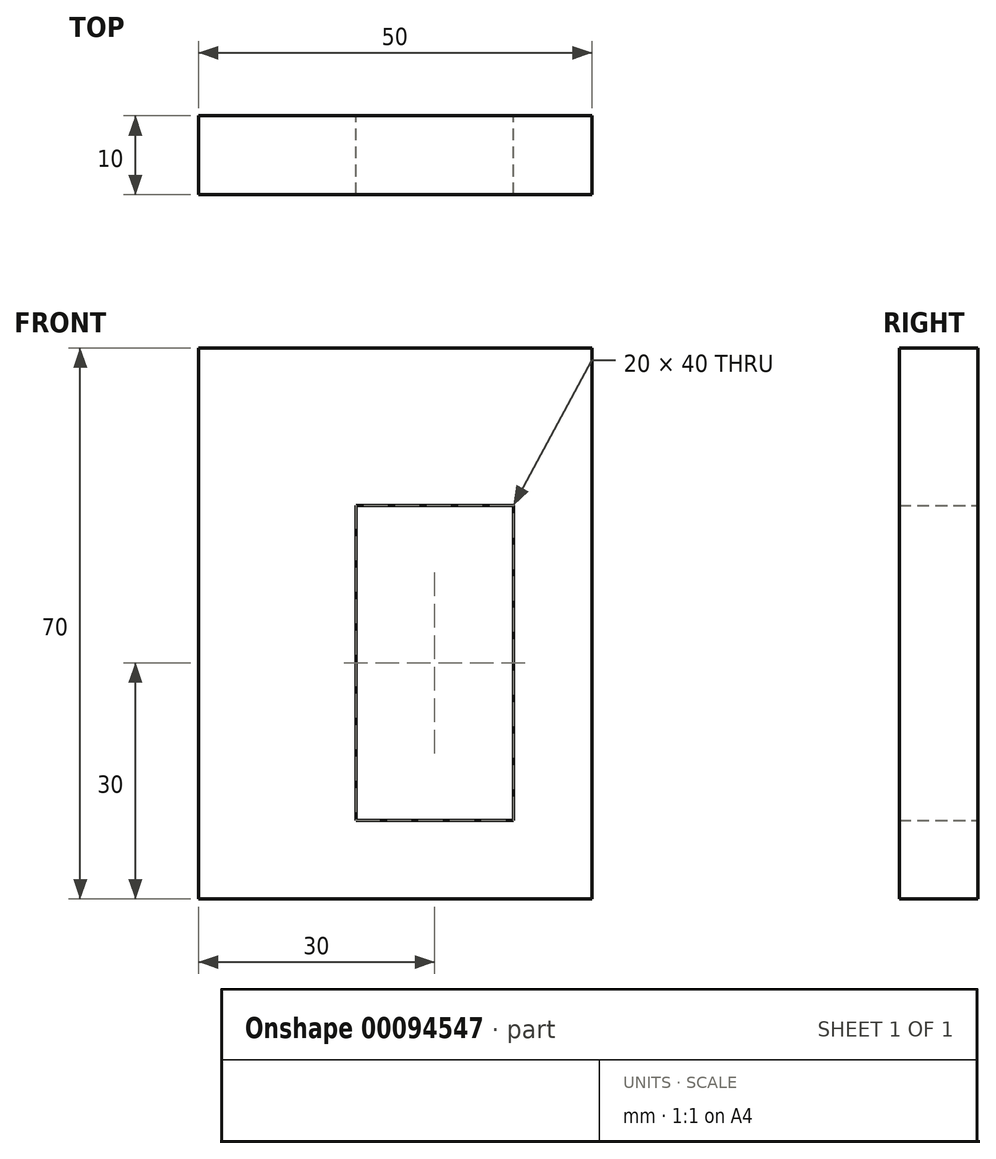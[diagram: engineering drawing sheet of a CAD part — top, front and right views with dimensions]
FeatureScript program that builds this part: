
annotation { "Feature Type Name" : "Feature", "Feature Type Description" : "" }
export const myFeature = defineFeature(function(context is Context, id is Id, definition is map)
    precondition{}
    {
        {
            var Q0;
            Q0=qCreatedBy(makeId("Front.planeOp"),FACE);
            var sketch = newSketch(context, id + "F0", { "sketchPlane" : qUnion([Q0])});
            skLineSegment(sketch, "E0.bottom", {"start": v(0, 0) * mm, "end": v(50, 0) * mm});
            skLineSegment(sketch, "E0.top", {"start": v(0, -70) * mm, "end": v(50, -70) * mm});
            skLineSegment(sketch, "E0.left", {"start": v(0, 0) * mm, "end": v(0, -70) * mm});
            skLineSegment(sketch, "E0.right", {"start": v(50, 0) * mm, "end": v(50, -70) * mm});
            skLineSegment(sketch, "E1.bottom", {"start": v(20, -60) * mm, "end": v(40, -60) * mm});
            skLineSegment(sketch, "E1.top", {"start": v(20, -20) * mm, "end": v(40, -20) * mm});
            skLineSegment(sketch, "E1.left", {"start": v(20, -60) * mm, "end": v(20, -20) * mm});
            skLineSegment(sketch, "E1.right", {"start": v(40, -60) * mm, "end": v(40, -20) * mm});
            skSolve(sketch);
        }
        {
            var Q0;
            Q0=makeQuery(id+"F0.imprint","IMPRINT",FACE,{"disambiguationData":[TD([[makeQuery(id+"F0.imprint","IMPRINT",EDGE,{"derivedFrom":sQuery(id+"F0.wireOp",EDGE,"E0.bottom")}),-1.0]])]});
            var Q1;
            Q1=makeQuery(id+"F0.imprint","IMPRINT",FACE,{"disambiguationData":[TD([[makeQuery(id+"F0.imprint","IMPRINT",EDGE,{"derivedFrom":sQuery(id+"F0.wireOp",EDGE,"E0.bottom")}),-1.0]])]});
            extrude(context, id + "F1", {"entities" : qUnion([Q0, Q1]), "depth" : 10 * mm});
        }
        {
            var Q0;
            Q0 = qSketchRegion(id + "F0", true);
            extrude(context, id + "F2", {"entities" : qUnion([Q0]), "operationType" : NewBodyOperationType.ADD, "depth" : 10 * mm});
        }
    });
